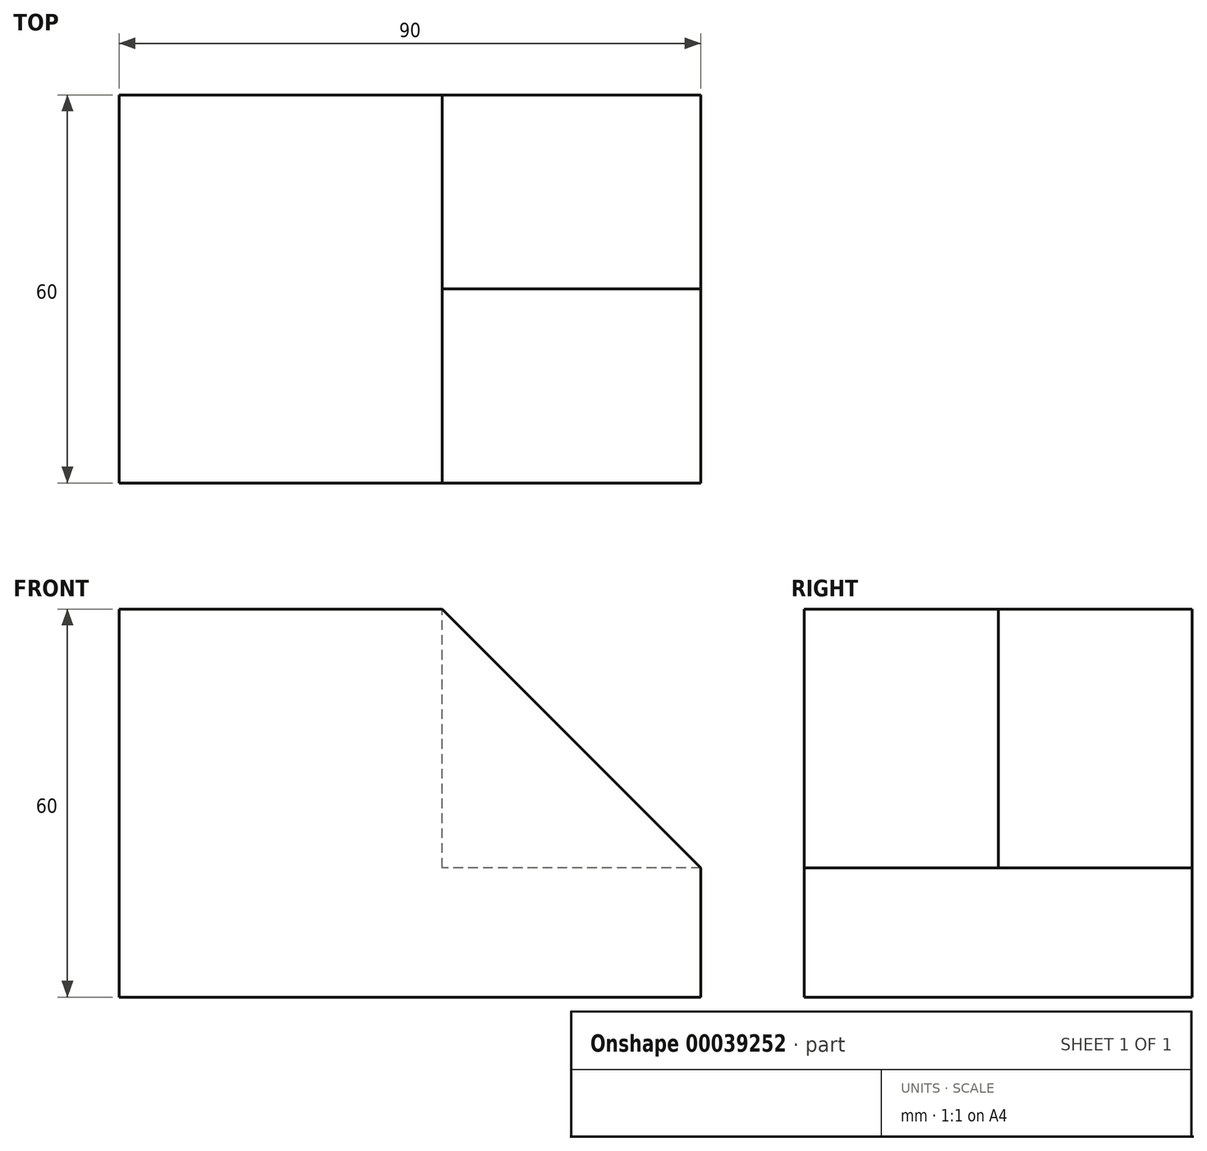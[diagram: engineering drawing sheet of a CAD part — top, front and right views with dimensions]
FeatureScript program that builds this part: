
annotation { "Feature Type Name" : "Feature", "Feature Type Description" : "" }
export const myFeature = defineFeature(function(context is Context, id is Id, definition is map)
    precondition{}
    {
        {
            var Q0;
            Q0=qCreatedBy(makeId("Front.planeOp"),FACE);
            var sketch = newSketch(context, id + "F0", { "sketchPlane" : qUnion([Q0])});
            skLineSegment(sketch, "E0.bottom", {"start": v(-47.95, 47.76) * mm, "end": v(2.05, 47.76) * mm});
            skLineSegment(sketch, "E0.top", {"start": v(-47.95, -12.24) * mm, "end": v(42.05, -12.24) * mm});
            skLineSegment(sketch, "E0.left", {"start": v(-47.95, 47.76) * mm, "end": v(-47.95, -12.24) * mm});
            skLineSegment(sketch, "E0.right", {"start": v(42.05, 7.76) * mm, "end": v(42.05, -12.24) * mm});
            skLineSegment(sketch, "E1", {"start": v(42.05, 7.76) * mm, "end": v(2.05, 47.76) * mm});
            skSolve(sketch);
        }
        {
            var Q0;
            Q0=makeQuery(id+"F0.imprint","IMPRINT",FACE,{"disambiguationData":[TD([[makeQuery(id+"F0.imprint","IMPRINT",EDGE,{"derivedFrom":sQuery(id+"F0.wireOp",EDGE,"E0.bottom")}),-1.0]])]});
            extrude(context, id + "F1", {"entities" : qUnion([Q0]), "depth" : 60 * mm});
        }
        {
            var Q0;
            Q0=makeQuery(id+"F1.opExtrude","CAP_FACE",FACE,{"disambiguationData":[OSD([sQuery(id+"F0.wireOp",EDGE,"E0.bottom"),sQuery(id+"F0.wireOp",EDGE,"E0.top"),sQuery(id+"F0.wireOp",EDGE,"E0.left"),sQuery(id+"F0.wireOp",EDGE,"E0.right"),sQuery(id+"F0.wireOp",EDGE,"E1")])],"isStart":true});
            var sketch = newSketch(context, id + "F2", { "sketchPlane" : qUnion([Q0])});
            skLineSegment(sketch, "E2", {"start": v(-42.05, 7.76) * mm, "end": v(-2.05, 7.76) * mm});
            skLineSegment(sketch, "E3", {"start": v(-2.05, 7.76) * mm, "end": v(-2.05, 47.76) * mm});
            skSolve(sketch);
        }
        {
            var Q0;
            Q0=makeQuery(id+"F2.imprint","IMPRINT",FACE,{"disambiguationData":[TD([[makeQuery(id+"F2.imprint","IMPRINT",EDGE,{"derivedFrom":sQuery(id+"F2.wireOp",EDGE,"E2")}),1.0]])]});
            extrude(context, id + "F3", {"entities" : qUnion([Q0]), "operationType" : NewBodyOperationType.REMOVE, "oppositeDirection" : true, "depth" : 30 * mm});
        }
    });
